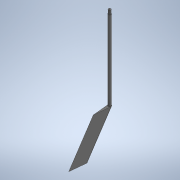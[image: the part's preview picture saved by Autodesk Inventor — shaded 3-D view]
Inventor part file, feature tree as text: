
AUTODESK INVENTOR PART (.ipt)
format: ipt  version: 2020 (Build 240168000, 168)  size: 120,832 bytes
history: native  units: mm
features: sketch x4, extrude x2, sweep x1, thread x1
ambient origin geometry x8: Origin, YZ Plane, XZ Plane, XY Plane, X Axis, Y Axis, Z Axis, Center Point
bodies: Solid1 (feature_tree)
feature tree (8):
  sweep  "Sweep1"
  extrude  "Extrusion1"  Depth=90.0mm
  extrude  "Extrusion2"  Depth=204.0mm
  thread  "Thread1"  [1 undecoded]
  sketch  "Sketch1"  dims[d0=4.0mm d1=40.0mm]
  sketch  "Sketch2"  dims[d2=90.0mm d3=60.0mm]
  sketch  "Sketch3"  dims[d4=0.0mm d5=0.0mm d6=7.0mm d7=204.0mm d8=0.0mm]
  sketch  "Sketch4"  dims[d9=6.0mm d10=10.0mm d11=1.0mm d12=10.0mm d13=10.0mm d14=0.0mm d15=10.0mm d16=0.0mm]
note: 1 required parameter value undecoded (feature->parameter linkage not recoverable at this tier; creation-order binding heuristic only, values carry confidence <= 0.55)
